# Revit family: Table-Teknion-CFTSTH_Figure_Table_Rectangular_Hexa_Panel_Base_Subtop-R2023
name_source: partatom
category: Furniture
units: mm (PartAtom-declared; Revit-internal decimal feet)

## family parameters
Always vertical = Yes
Cut with Voids When Loaded = No
Enable Cutting in Views = No
OmniClass Number = 23.40.20.00
OmniClass Title = General Furniture and Specialties
Render Appearance Source = Family Geometry
Room Calculation Point = No
Shared = Yes
Work Plane-Based = No

## types (3) — shared parameters
Assembly Code = E2020200
Central Base With Wire Management = Select Only One Central Base Option Below
Manufacturer = Teknion
Manufacturer Fax = 416.661.4586
Part Number = CFTSTH
Product Documentation Link = https://d2r72yk5wmppdj.cloudfront.net
Product Line = Figure Table
Product Page URL = https://www.teknion.com
Series = Custom Wood Boardroom & Reception Tables
Sustainability Data = https://www.teknion.com
URL = www.teknion.com
Unit Weight URL = http://www.teknion.com
Warranty = http://www.teknion.com
zero-valued in all types: Default Elevation

## per-type parameters (varying)
| type | Cut - Central Base - Hexa | Cut - Central Base - Softened | Description | H - Hexa Panel | Model | N - No Central Base | S - Softened Panel |
| No Central Base | 0.3 " | 0.3 " | Figure Table, Rectangular, Hexa Panel Base, Subtop, No Central Base | No | CFTSTH_____N | Yes | No |
| Softened Panel Central Base | 0.3 " | 15 " | Figure Table, Rectangular, Hexa Panel Base, Subtop , Softened Panel Central Base | No | CFTSTH_____S | No | Yes |
| Hexa Panel Central Base | 15 " | 0.3 " | Figure Table, Rectangular, Hexa Panel Base, Subtop , Hexa Panel Central Base | Yes | CFTSTH_____H | No | No |

## geometry (parser evidence)
native form markers: Sweep x6
no freeform markers — native parametric forms only
